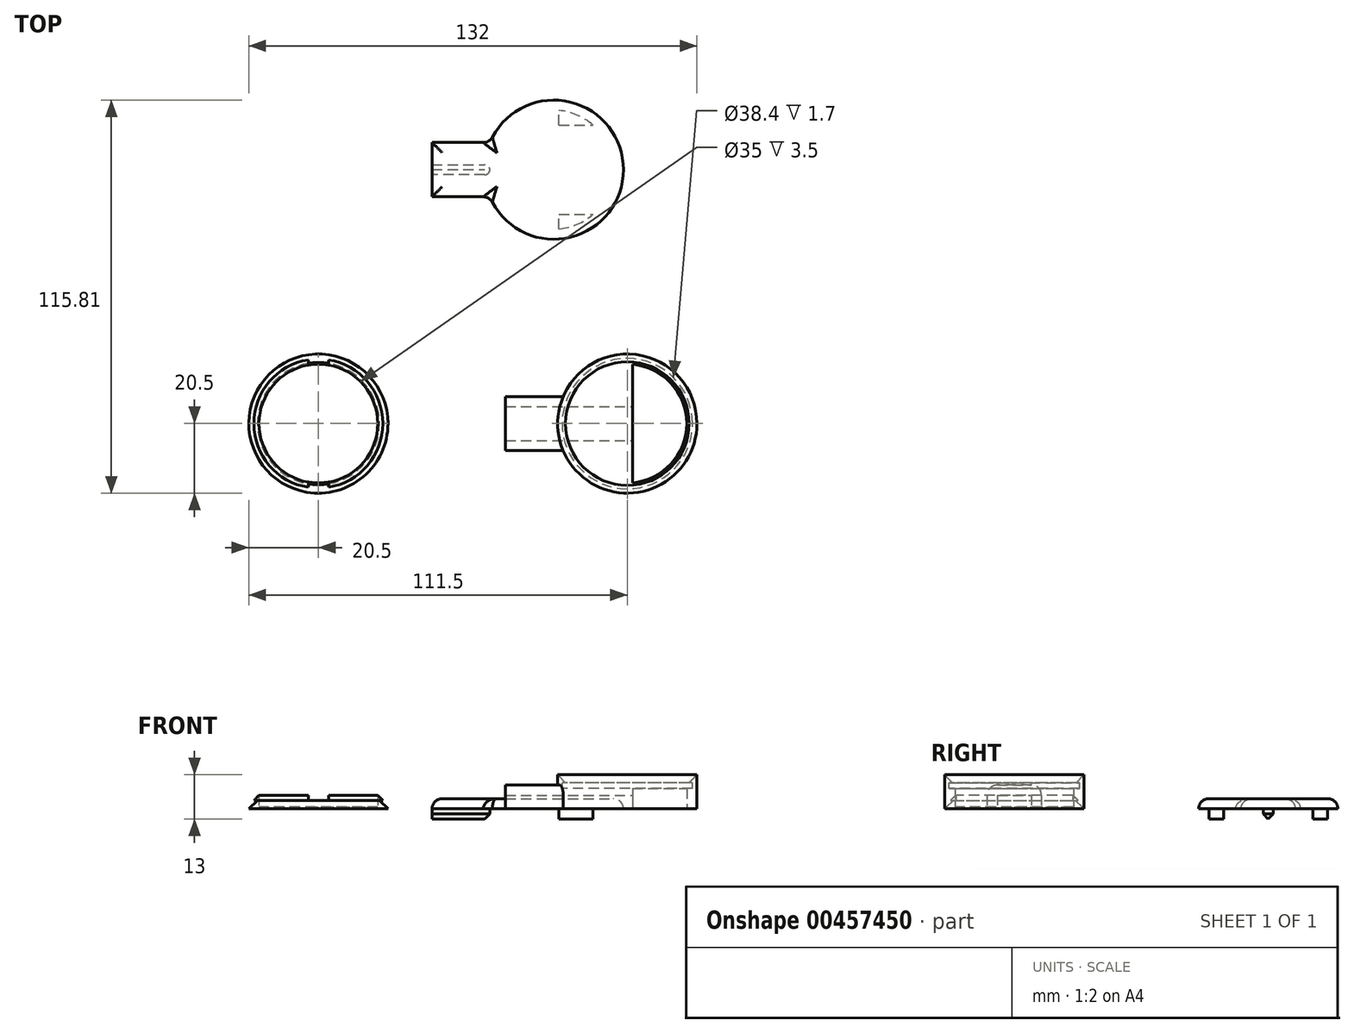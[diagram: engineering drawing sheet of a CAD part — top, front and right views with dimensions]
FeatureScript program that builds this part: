
annotation { "Feature Type Name" : "Feature", "Feature Type Description" : "" }
export const myFeature = defineFeature(function(context is Context, id is Id, definition is map)
    precondition{}
    {
        {
            var Q0;
            Q0=qCreatedBy(makeId("Top.planeOp"),FACE);
            var sketch = newSketch(context, id + "F0", { "sketchPlane" : qUnion([Q0])});
            skCircle(sketch, "E0", {"center": v(0, 0) * mm, "radius": 17.5 * mm});
            skSolve(sketch);
        }
        {
            var Q0;
            Q0 = qSketchRegion(id + "F0", true);
            extrude(context, id + "F1", {"entities" : qUnion([Q0]), "depth" : 0.5 * mm});
        }
        {
            var Q0;
            Q0=qCreatedBy(makeId("Top.planeOp"),FACE);
            var sketch = newSketch(context, id + "F2", { "sketchPlane" : qUnion([Q0])});
            skCircle(sketch, "E1", {"center": v(0, 0) * mm, "radius": 20.5 * mm});
            skCircle(sketch, "E2.0", {"center": v(0, 0) * mm, "radius": 17.5 * mm});
            skSolve(sketch);
        }
        {
            var Q0;
            Q0 = qSketchRegion(id + "F2", true);
            extrude(context, id + "F3", {"entities" : qUnion([Q0]), "operationType" : NewBodyOperationType.ADD, "depth" : 4 * mm});
        }
        {
            var Q0;
            Q0=qCreatedBy(makeId("Front.planeOp"),FACE);
            var sketch = newSketch(context, id + "F4", { "sketchPlane" : qUnion([Q0])});
            skLineSegment(sketch, "E3", {"start": v(-20.5, 0) * mm, "end": v(-20.5, 4) * mm});
            skLineSegment(sketch, "E4", {"start": v(20.5, 4) * mm, "end": v(20.5, 0) * mm});
            skLineSegment(sketch, "E5", {"start": v(-20.5, 4) * mm, "end": v(-19, 4) * mm});
            skLineSegment(sketch, "E6", {"start": v(-19, 2.5) * mm, "end": v(-18, 2.5) * mm});
            skLineSegment(sketch, "E7", {"start": v(-20.5, 0) * mm, "end": v(-18, 2.5) * mm});
            skLineSegment(sketch, "E8", {"start": v(-19, 2.5) * mm, "end": v(-17.5, 4) * mm});
            skLineSegment(sketch, "E9", {"start": v(-19, 4) * mm, "end": v(-17.5, 4) * mm});
            skSolve(sketch);
        }
        {
            var Q0;
            Q0 = qSketchRegion(id + "F4", true);
            var Q1;
            Q1=makeQuery(id+"F3.opExtrude","CAP_EDGE",EDGE,{"disambiguationData":[OSD([sQuery(id+"F2.wireOp",EDGE,"E2.0")])],"isStart":false});
            revolve(context, id + "F5", {"operationType" : NewBodyOperationType.REMOVE, "entities" : qUnion([Q0]), "axis" : qUnion([Q1]), "revolveType" : RevolveType.FULL, "oppositeDirection" : true});
        }
        {
            var Q0;
            Q0=qCreatedBy(makeId("Top.planeOp"),FACE);
            var sketch = newSketch(context, id + "F6", { "sketchPlane" : qUnion([Q0])});
            skCircle(sketch, "E10", {"center": v(91, 0) * mm, "radius": 20.5 * mm});
            skLineSegment(sketch, "E11", {"start": v(92.5, -17.44) * mm, "end": v(92.5, 17.44) * mm});
            skArc(sketch, "E12", {"start": v(92.5, 17.44) * mm, "mid": v(108.5, 0) * mm, "end": v(92.5, -17.44) * mm});
            skSolve(sketch);
        }
        {
            var Q0;
            Q0 = qSketchRegion(id + "F6", true);
            extrude(context, id + "F7", {"entities" : qUnion([Q0]), "depth" : 6 * mm});
        }
        {
            var Q0;
            Q0=makeQuery(id+"F7.opExtrude","CAP_FACE",FACE,{"disambiguationData":[OSD([sQuery(id+"F6.wireOp",EDGE,"E10"),sQuery(id+"F6.wireOp",EDGE,"E11"),sQuery(id+"F6.wireOp",EDGE,"E12")])],"isStart":false});
            var sketch = newSketch(context, id + "F8", { "sketchPlane" : qUnion([Q0])});
            skCircle(sketch, "E13", {"center": v(91, 0) * mm, "radius": 17.5 * mm});
            skCircle(sketch, "E14.0", {"center": v(91, 0) * mm, "radius": 20.5 * mm});
            skSolve(sketch);
        }
        {
            var Q0;
            Q0 = qSketchRegion(id + "F8", true);
            extrude(context, id + "F9", {"entities" : qUnion([Q0]), "operationType" : NewBodyOperationType.ADD, "depth" : 4 * mm});
        }
        {
            var Q0;
            Q0=qCreatedBy(makeId("Front.planeOp"),FACE);
            var sketch = newSketch(context, id + "F10", { "sketchPlane" : qUnion([Q0])});
            skPoint(sketch, "E15.0.1.start.orphan", {"position": v(92.5, 6) * mm});
            skPoint(sketch, "E16.0.end.orphan", {"position": v(108.5, 10) * mm});
            skLineSegment(sketch, "E17", {"start": v(70.5, 0) * mm, "end": v(70.5, 10) * mm});
            skLineSegment(sketch, "E18.0", {"start": v(70.5, 10) * mm, "end": v(111.5, 10) * mm});
            skLineSegment(sketch, "E19", {"start": v(111.5, 10) * mm, "end": v(111.5, 0) * mm});
            skLineSegment(sketch, "E20", {"start": v(70.5, 10) * mm, "end": v(72.8, 7.7) * mm});
            skLineSegment(sketch, "E21", {"start": v(72.8, 7.7) * mm, "end": v(71.8, 7.7) * mm});
            skLineSegment(sketch, "E22", {"start": v(71.8, 7.7) * mm, "end": v(71.8, 6) * mm});
            skLineSegment(sketch, "E23.0", {"start": v(92.5, 6) * mm, "end": v(73.5, 6) * mm});
            skLineSegment(sketch, "E24", {"start": v(73.5, 6) * mm, "end": v(71.8, 6) * mm});
            skLineSegment(sketch, "E25", {"start": v(73.5, 6) * mm, "end": v(73.5, 10) * mm});
            skPoint(sketch, "E26.orphan", {"position": v(73, 10) * mm});
            skPoint(sketch, "E27.end.orphan", {"position": v(72.8, 4.76) * mm});
            skSolve(sketch);
        }
        {
            var Q0;
            Q0 = qSketchRegion(id + "F10", true);
            var Q1;
            Q1=makeQuery(id+"F9.opExtrude","CAP_EDGE",EDGE,{"disambiguationData":[OSD([sQuery(id+"F8.wireOp",EDGE,"E13")])],"isStart":false});
            revolve(context, id + "F11", {"operationType" : NewBodyOperationType.REMOVE, "entities" : qUnion([Q0]), "axis" : qUnion([Q1]), "revolveType" : RevolveType.FULL, "oppositeDirection" : true});
        }
        {
            var Q0;
            Q0=makeQuery(id+"F7.opExtrude","CAP_FACE",FACE,{"disambiguationData":[OSD([sQuery(id+"F6.wireOp",EDGE,"E10"),sQuery(id+"F6.wireOp",EDGE,"E11"),sQuery(id+"F6.wireOp",EDGE,"E12")])],"isStart":true});
            var sketch = newSketch(context, id + "F12", { "sketchPlane" : qUnion([Q0])});
            skLineSegment(sketch, "E28", {"start": v(71.12, 5) * mm, "end": v(92.5, 5) * mm});
            skLineSegment(sketch, "E29", {"start": v(71.12, -5) * mm, "end": v(92.5, -5) * mm});
            skArc(sketch, "E30.0.0", {"start": v(71.12, 5) * mm, "mid": v(70.5, 0) * mm, "end": v(71.12, -5) * mm});
            skLineSegment(sketch, "E31", {"start": v(92.5, -5) * mm, "end": v(92.5, 5) * mm});
            skSolve(sketch);
        }
        {
            var Q0;
            Q0 = qSketchRegion(id + "F12", true);
            extrude(context, id + "F13", {"entities" : qUnion([Q0]), "operationType" : NewBodyOperationType.REMOVE, "oppositeDirection" : true, "depth" : 4 * mm});
        }
        {
            var Q0;
            Q0=makeQuery(id+"F7.opExtrude","CAP_FACE",FACE,{"disambiguationData":[OSD([sQuery(id+"F6.wireOp",EDGE,"E10"),sQuery(id+"F6.wireOp",EDGE,"E11"),sQuery(id+"F6.wireOp",EDGE,"E12")])],"isStart":true});
            var sketch = newSketch(context, id + "F14", { "sketchPlane" : qUnion([Q0])});
            skArc(sketch, "E32.0", {"start": v(71.12, 5) * mm, "mid": v(111.5, 0) * mm, "end": v(71.12, -5) * mm});
            skLineSegment(sketch, "E33", {"start": v(72.13, 8) * mm, "end": v(55.12, 8) * mm});
            skLineSegment(sketch, "E34", {"start": v(55.12, 8) * mm, "end": v(55.12, 5) * mm});
            skLineSegment(sketch, "E35", {"start": v(55.12, -8) * mm, "end": v(72.13, -8) * mm});
            skLineSegment(sketch, "E36", {"start": v(71.12, 5) * mm, "end": v(55.12, 5) * mm});
            skLineSegment(sketch, "E37", {"start": v(71.12, -5) * mm, "end": v(55.12, -5) * mm});
            skLineSegment(sketch, "E38.trimOffspring", {"start": v(55.12, -5) * mm, "end": v(55.12, -8) * mm});
            skSolve(sketch);
        }
        {
            var Q0;
            Q0 = qSketchRegion(id + "F14", true);
            extrude(context, id + "F15", {"entities" : qUnion([Q0]), "operationType" : NewBodyOperationType.ADD, "oppositeDirection" : true, "depth" : 4 * mm});
        }
        {
            var Q0;
            Q0=makeQuery(id+"F15.opExtrude","CAP_FACE",FACE,{"disambiguationData":[OSD([sQuery(id+"F14.wireOp",EDGE,"E32.0"),sQuery(id+"F14.wireOp",EDGE,"E33"),sQuery(id+"F14.wireOp",EDGE,"E34"),sQuery(id+"F14.wireOp",EDGE,"E36")])],"isStart":false});
            var sketch = newSketch(context, id + "F16", { "sketchPlane" : qUnion([Q0])});
            skLineSegment(sketch, "E39.0.1", {"start": v(55.12, -5) * mm, "end": v(55.12, -8) * mm});
            skLineSegment(sketch, "E39.0.2", {"start": v(55.12, -8) * mm, "end": v(72.13, -8) * mm});
            skArc(sketch, "E39.0.3", {"start": v(72.13, -8) * mm, "mid": v(71.56, -6.52) * mm, "end": v(71.12, -5) * mm});
            skArc(sketch, "E40.0.0", {"start": v(71.12, 5) * mm, "mid": v(71.56, 6.52) * mm, "end": v(72.13, 8) * mm});
            skLineSegment(sketch, "E40.0.1", {"start": v(72.13, 8) * mm, "end": v(55.12, 8) * mm});
            skLineSegment(sketch, "E40.0.2", {"start": v(55.12, 8) * mm, "end": v(55.12, 5) * mm});
            skLineSegment(sketch, "E41", {"start": v(55.12, -5) * mm, "end": v(55.12, 5) * mm});
            skArc(sketch, "E42", {"start": v(71.12, -5) * mm, "mid": v(70.5, 0) * mm, "end": v(71.12, 5) * mm});
            skSolve(sketch);
        }
        {
            var Q0;
            Q0 = qSketchRegion(id + "F16", true);
            extrude(context, id + "F17", {"entities" : qUnion([Q0]), "operationType" : NewBodyOperationType.ADD, "depth" : 3 * mm});
        }
        {
            var Q0;
            Q0=makeQuery(id+"F17.boolean.opBoolean","MERGE",EDGE,{"derivedFrom":[makeQuery(id+"F15.opExtrude","SWEPT_EDGE",EDGE,{"disambiguationData":[OSD([sQuery(id+"F14.wireOp",EDGE,"E32.0"),sQuery(id+"F14.wireOp",EDGE,"E33")])]}),makeQuery(id+"F17.opExtrude","SWEPT_EDGE",EDGE,{"disambiguationData":[OSD([sQuery(id+"F16.wireOp",EDGE,"E39.0.2"),sQuery(id+"F16.wireOp",EDGE,"E39.0.3")])]})]});
            var Q1;
            Q1=makeQuery(id+"F17.opExtrude","CAP_EDGE",EDGE,{"disambiguationData":[OSD([sQuery(id+"F16.wireOp",EDGE,"E39.0.3"),sQuery(id+"F16.wireOp",EDGE,"E40.0.0"),sQuery(id+"F16.wireOp",EDGE,"E42")])],"isStart":false});
            var Q2;
            Q2=makeQuery(id+"F17.boolean.opBoolean","MERGE",EDGE,{"derivedFrom":[makeQuery(id+"F15.opExtrude","SWEPT_EDGE",EDGE,{"disambiguationData":[OSD([sQuery(id+"F14.wireOp",EDGE,"E32.0"),sQuery(id+"F14.wireOp",EDGE,"E35")])]}),makeQuery(id+"F17.opExtrude","SWEPT_EDGE",EDGE,{"disambiguationData":[OSD([sQuery(id+"F16.wireOp",EDGE,"E40.0.0"),sQuery(id+"F16.wireOp",EDGE,"E40.0.1")])]})]});
            var Q3;
            Q3=makeQuery(id+"F17.opExtrude","CAP_EDGE",EDGE,{"disambiguationData":[OSD([sQuery(id+"F16.wireOp",EDGE,"E39.0.2")])],"isStart":false});
            var Q4;
            Q4=makeQuery(id+"F17.opExtrude","CAP_EDGE",EDGE,{"disambiguationData":[OSD([sQuery(id+"F16.wireOp",EDGE,"E40.0.1")])],"isStart":false});
            fillet(context, id + "F18", {"entities" : qUnion([Q0, Q1, Q2, Q3, Q4]), "radius" : 3 * mm, "tangentPropagation" : true, "allowEdgeOverflow" : false});
        }
        {
            var Q0;
            Q0=qCreatedBy(makeId("Front.planeOp"),FACE);
            var sketch = newSketch(context, id + "F19", { "sketchPlane" : qUnion([Q0])});
            skLineSegment(sketch, "E43.0", {"start": v(-3, 4) * mm, "end": v(3, 4) * mm});
            skLineSegment(sketch, "E44.0", {"start": v(-3, 2.5) * mm, "end": v(3, 2.5) * mm});
            skLineSegment(sketch, "E45", {"start": v(-3, 4) * mm, "end": v(-3, 2.5) * mm});
            skLineSegment(sketch, "E46", {"start": v(3, 4) * mm, "end": v(3, 2.5) * mm});
            skPoint(sketch, "E47.orphan", {"position": v(-17.5, 4) * mm});
            skPoint(sketch, "E48.orphan", {"position": v(-19, 2.5) * mm});
            skPoint(sketch, "E49.orphan", {"position": v(19, 2.5) * mm});
            skPoint(sketch, "E50.orphan", {"position": v(17.5, 4) * mm});
            skSolve(sketch);
        }
        {
            var Q0;
            Q0 = qSketchRegion(id + "F19", true);
            extrude(context, id + "F20", {"entities" : qUnion([Q0]), "operationType" : NewBodyOperationType.REMOVE, "endBound" : BoundingType.THROUGH_ALL, "depth" : 25 * mm, "hasSecondDirection" : true, "secondDirectionBound" : SecondDirectionBoundingType.THROUGH_ALL, "secondDirectionOppositeDirection" : true, "secondDirectionDepth" : 25 * mm});
        }
        {
            var Q0;
            Q0=qCreatedBy(makeId("Top.planeOp"),FACE);
            var sketch = newSketch(context, id + "F21", { "sketchPlane" : qUnion([Q0])});
            skArc(sketch, "E51", {"start": v(50.49, 66.81) * mm, "mid": v(89.86, 74.81) * mm, "end": v(50.49, 82.81) * mm});
            skLineSegment(sketch, "E52", {"start": v(50.49, 66.81) * mm, "end": v(33.49, 66.81) * mm});
            skLineSegment(sketch, "E53", {"start": v(33.49, 66.81) * mm, "end": v(33.49, 82.81) * mm});
            skLineSegment(sketch, "E54", {"start": v(33.49, 82.81) * mm, "end": v(50.49, 82.81) * mm});
            skPoint(sketch, "E55.orphan", {"position": v(69.36, 66.81) * mm});
            skPoint(sketch, "E56.orphan", {"position": v(69.36, 82.81) * mm});
            skSolve(sketch);
        }
        {
            var Q0;
            Q0 = qSketchRegion(id + "F21", true);
            extrude(context, id + "F22", {"entities" : qUnion([Q0]), "depth" : 3 * mm});
        }
        {
            var Q0;
            Q0=makeQuery(id+"F22.opExtrude","CAP_FACE",FACE,{"disambiguationData":[OSD([sQuery(id+"F21.wireOp",EDGE,"E51"),sQuery(id+"F21.wireOp",EDGE,"E52"),sQuery(id+"F21.wireOp",EDGE,"E53"),sQuery(id+"F21.wireOp",EDGE,"E54")])],"isStart":false});
            fillet(context, id + "F23", {"entities" : qUnion([Q0]), "radius" : 3 * mm, "tangentPropagation" : true, "allowEdgeOverflow" : false});
        }
        {
            var Q0;
            Q0=makeQuery(id+"F22.opExtrude","CAP_FACE",FACE,{"disambiguationData":[OSD([sQuery(id+"F21.wireOp",EDGE,"E51"),sQuery(id+"F21.wireOp",EDGE,"E52"),sQuery(id+"F21.wireOp",EDGE,"E53"),sQuery(id+"F21.wireOp",EDGE,"E54")])],"isStart":true});
            var sketch = newSketch(context, id + "F24", { "sketchPlane" : qUnion([Q0])});
            skArc(sketch, "E57", {"start": v(70.86, -92.25) * mm, "mid": v(76.2, -90.92) * mm, "end": v(80.86, -88) * mm});
            skLineSegment(sketch, "E58", {"start": v(70.86, -57.38) * mm, "end": v(70.86, -61.62) * mm});
            skLineSegment(sketch, "E59", {"start": v(70.86, -61.62) * mm, "end": v(80.86, -61.62) * mm});
            skLineSegment(sketch, "E60", {"start": v(70.86, -88) * mm, "end": v(80.86, -88) * mm});
            skLineSegment(sketch, "E61.trimOffspring", {"start": v(70.86, -88) * mm, "end": v(70.86, -92.25) * mm});
            skArc(sketch, "E62.trimOffspring", {"start": v(80.86, -61.62) * mm, "mid": v(76.2, -58.7) * mm, "end": v(70.86, -57.38) * mm});
            skLineSegment(sketch, "E63", {"start": v(33.49, -74.81) * mm, "end": v(50.49, -74.81) * mm});
            skLineSegment(sketch, "E64", {"start": v(50.49, -74.81) * mm, "end": v(50.49, -73.31) * mm});
            skLineSegment(sketch, "E65", {"start": v(50.49, -73.31) * mm, "end": v(33.49, -73.31) * mm});
            skLineSegment(sketch, "E66", {"start": v(33.49, -73.31) * mm, "end": v(33.49, -76.31) * mm});
            skLineSegment(sketch, "E67", {"start": v(33.49, -76.31) * mm, "end": v(50.49, -76.31) * mm});
            skLineSegment(sketch, "E68", {"start": v(50.49, -76.31) * mm, "end": v(50.49, -74.81) * mm});
            skSolve(sketch);
        }
        {
            var Q0;
            Q0 = qSketchRegion(id + "F24", true);
            extrude(context, id + "F25", {"entities" : qUnion([Q0]), "operationType" : NewBodyOperationType.ADD, "depth" : 3 * mm});
        }
        {
            var Q0;
            Q0=makeQuery(id+"F25.opExtrude","SWEPT_EDGE",EDGE,{"disambiguationData":[OSD([sQuery(id+"F24.wireOp",EDGE,"E67"),sQuery(id+"F24.wireOp",EDGE,"E68")])]});
            var Q1;
            Q1=makeQuery(id+"F25.opExtrude","SWEPT_EDGE",EDGE,{"disambiguationData":[OSD([sQuery(id+"F24.wireOp",EDGE,"E64"),sQuery(id+"F24.wireOp",EDGE,"E65")])]});
            fillet(context, id + "F26", {"entities" : qUnion([Q0, Q1]), "radius" : 1.5 * mm, "tangentPropagation" : true, "allowEdgeOverflow" : false});
        }
        {
            var Q0;
            Q0=makeQuery(id+"F25.opExtrude","CAP_EDGE",EDGE,{"disambiguationData":[OSD([sQuery(id+"F24.wireOp",EDGE,"E65")])],"isStart":false});
            var Q1;
            Q1=makeQuery(id+"F25.opExtrude","CAP_EDGE",EDGE,{"disambiguationData":[OSD([sQuery(id+"F24.wireOp",EDGE,"E67")])],"isStart":false});
            chamfer(context, id + "F27", {"entities" : qUnion([Q0, Q1]), "width" : 1.5 * mm, "tangentPropagation" : true});
        }
        {
            var Q0;
            Q0=makeQuery(id+"F23.opFillet","BLEND_EDGE",EDGE,{"blendedFrom":[makeQuery(id+"F22.opExtrude","CAP_EDGE",EDGE,{"disambiguationData":[OSD([sQuery(id+"F21.wireOp",EDGE,"E51")])],"isStart":false}),makeQuery(id+"F22.opExtrude","CAP_EDGE",EDGE,{"disambiguationData":[OSD([sQuery(id+"F21.wireOp",EDGE,"E54")])],"isStart":false})],"blendedInto":[]});
            var Q1;
            Q1=makeQuery(id+"F23.opFillet","BLEND_EDGE",EDGE,{"blendedFrom":[makeQuery(id+"F22.opExtrude","CAP_EDGE",EDGE,{"disambiguationData":[OSD([sQuery(id+"F21.wireOp",EDGE,"E51")])],"isStart":false}),makeQuery(id+"F22.opExtrude","CAP_EDGE",EDGE,{"disambiguationData":[OSD([sQuery(id+"F21.wireOp",EDGE,"E52")])],"isStart":false})],"blendedInto":[]});
            fillet(context, id + "F28", {"entities" : qUnion([Q0, Q1]), "radius" : 3 * mm, "tangentPropagation" : true, "allowEdgeOverflow" : false});
        }
    });
